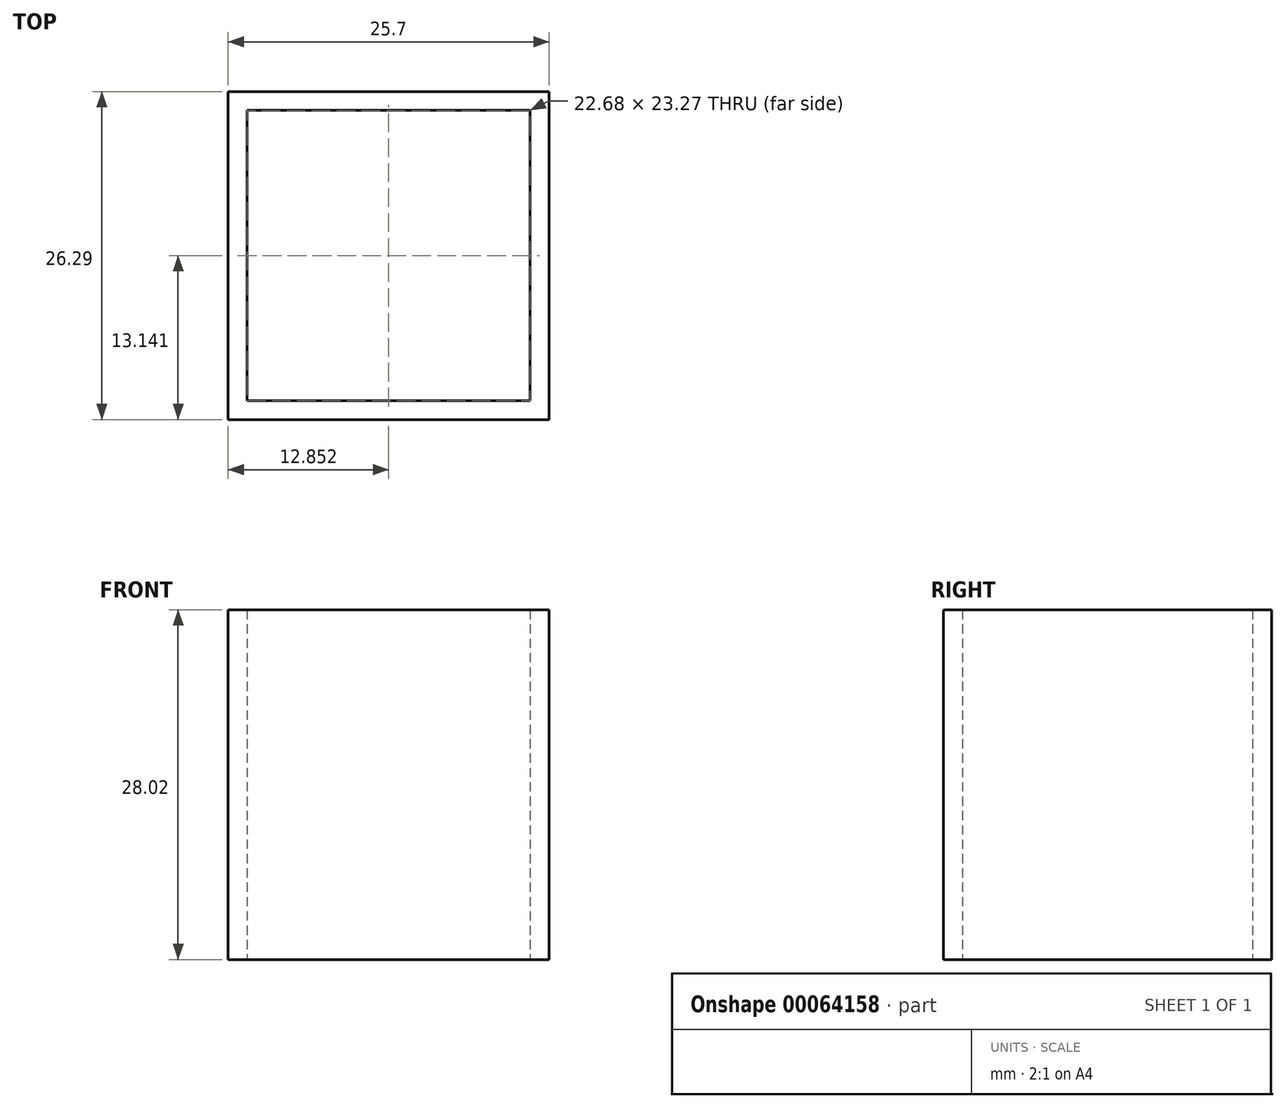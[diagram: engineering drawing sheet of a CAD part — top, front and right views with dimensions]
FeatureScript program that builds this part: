
annotation { "Feature Type Name" : "Feature", "Feature Type Description" : "" }
export const myFeature = defineFeature(function(context is Context, id is Id, definition is map)
    precondition{}
    {
        {
            var Q0;
            Q0=qCreatedBy(makeId("Top.planeOp"),FACE);
            var sketch = newSketch(context, id + "F0", { "sketchPlane" : qUnion([Q0])});
            skLineSegment(sketch, "E0.bottom", {"start": v(-26.82, 44.99) * mm, "end": v(-1.12, 44.99) * mm});
            skLineSegment(sketch, "E0.top", {"start": v(-26.82, 18.7) * mm, "end": v(-1.12, 18.7) * mm});
            skLineSegment(sketch, "E0.left", {"start": v(-26.82, 44.99) * mm, "end": v(-26.82, 18.7) * mm});
            skLineSegment(sketch, "E0.right", {"start": v(-1.12, 44.99) * mm, "end": v(-1.12, 18.7) * mm});
            skPoint(sketch, "E1", {"position": v(-26.82, 31.84) * mm});
            skPoint(sketch, "E2", {"position": v(-13.97, 44.99) * mm});
            skPoint(sketch, "E3", {"position": v(-13.97, 31.84) * mm});
            skLineSegment(sketch, "E4.rect.bottom", {"start": v(-2.63, 20.2) * mm, "end": v(-25.3, 20.2) * mm});
            skLineSegment(sketch, "E4.rect.top", {"start": v(-2.63, 43.47) * mm, "end": v(-25.3, 43.47) * mm});
            skLineSegment(sketch, "E4.rect.left", {"start": v(-2.63, 20.2) * mm, "end": v(-2.63, 43.47) * mm});
            skLineSegment(sketch, "E4.rect.right", {"start": v(-25.3, 20.2) * mm, "end": v(-25.3, 43.47) * mm});
            skSolve(sketch);
        }
        {
            var Q0;
            Q0 = qSketchRegion(id + "F0", true);
            extrude(context, id + "F1", {"entities" : qUnion([Q0]), "depth" : 28.02 * mm});
        }
    });
